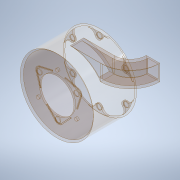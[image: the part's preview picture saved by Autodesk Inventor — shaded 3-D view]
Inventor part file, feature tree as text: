
AUTODESK INVENTOR PART (.ipt)
format: ipt  version: 2020 (Build 240168000, 168)  size: 402,944 bytes
history: native  units: in
note: dims shown in document units (in); Inventor stores cm internally (conversion verified against a paired STEP export)
features: sketch x11, extrude x8, projected_geometry x5, plane x2, shell x1, sweep x1, hole x1
ambient origin geometry x8: Origin, YZ Plane, XZ Plane, XY Plane, X Axis, Y Axis, Z Axis, Center Point
bodies: Solid1 (feature_tree)
feature tree (29):
  extrude  "Extrusion1"  Depth=3.1496in TaperAngle=0.0deg
  shell  "Shell1"  Thickness=0.1181in
  extrude  "Extrusion2"  Depth=3.1496in TaperAngle=0.0deg
  extrude  "Extrusion3"  Depth=1.5748in
  plane  "Work Plane1"
  extrude  "Extrusion4"  TaperAngle=120.0deg  [1 undecoded]
  extrude  "Extrusion5"  Depth=0.378in
  plane  "Work Plane4"
  sweep  "Sweep2"
  extrude  "Extrusion6"  [1 undecoded]
  extrude  "Extrusion7"  Depth=0.9843in TaperAngle=0.0deg
  extrude  "Extrusion8"  Depth=0.1181in TaperAngle=0.0deg
  hole  "Hole1"  [1 undecoded]
  sketch  "Sketch1"  dims[d1=5.3543in d2=3.1496in d3=0.0in d4=0.1181in]
  sketch  "Sketch2"  dims[d5=2.5197in d6=3.1496in d7=0.0in]
  sketch  "Sketch3"  dims[d8=0.378in d9=1.5748in]
  projected_geometry  "Projected Loop1"
  sketch  "Sketch4"  dims[d10=120.0deg d11=120.0deg]
  sketch  "Sketch6"  dims[d12=0.378in d13=0.378in]
  projected_geometry  "Projected Loop3"
  sketch  "Sketch9"  dims[d14=1.5748in d15=1.5748in]
  projected_geometry  "Projected Loop4"
  sketch  "Sketch10"  dims[d16=0.06in d17=0.0in d18=-0.9843in]
  sketch  "Sketch11"  dims[d24=1.1811in d25=0.9843in d26=0.0in]
  projected_geometry  "Projected Loop5"
  sketch  "Sketch12"  dims[d27=0.1181in d28=2.2201in d29=0.0in]
  projected_geometry  "Projected Loop6"
  sketch  "Sketch13"  dims[d37=0.0in d38=0.0in d39=0.0591in]
  sketch  "Sketch14"  dims[d40=0.0591in d41=0.0591in d42=0.0591in d43=0.0591in d44=0.0591in d45=0.0591in d46=0.9843in d47=0.9843in d48=0.9843in d49=0.9843in d50=0.9843in d51=0.9843in d52=0.0591in d53=0.0in d54=120.0deg d55=120.0deg d56=120.0deg d57=120.0deg d58=0.378in d59=0.378in d60=0.378in d61=0.378in d62=0.378in d63=0.378in d64=2.2638in d65=2.2638in d66=2.2638in d67=2.2638in d68=2.2638in d69=2.2638in d70=0.0591in d71=0.0591in d72=0.0591in d73=0.0591in d74=0.0591in d75=0.0591in d76=0.7874in d77=0.7874in d78=0.7874in d79=0.7874in d80=0.7874in d81=0.7874in d82=0.7874in d83=0.7874in d84=0.7874in d85=0.7874in d86=0.7874in d87=0.7874in d88=0.1181in d89=0.0in d90=0.378in d91=2.2638in d92=2.3622in d94=360.0deg d96=0.06in d97=0.0in d98=0.2362in d99=1.6142in d100=1.1811in d102=360.0deg d104=0.2362in d105=0.2362in d106=0.1575in d107=0.0787in d108=90.0deg d109=0.315in d110=0.8108in]
note: 3 required parameter values undecoded (feature->parameter linkage not recoverable at this tier; creation-order binding heuristic only, values carry confidence <= 0.55)
